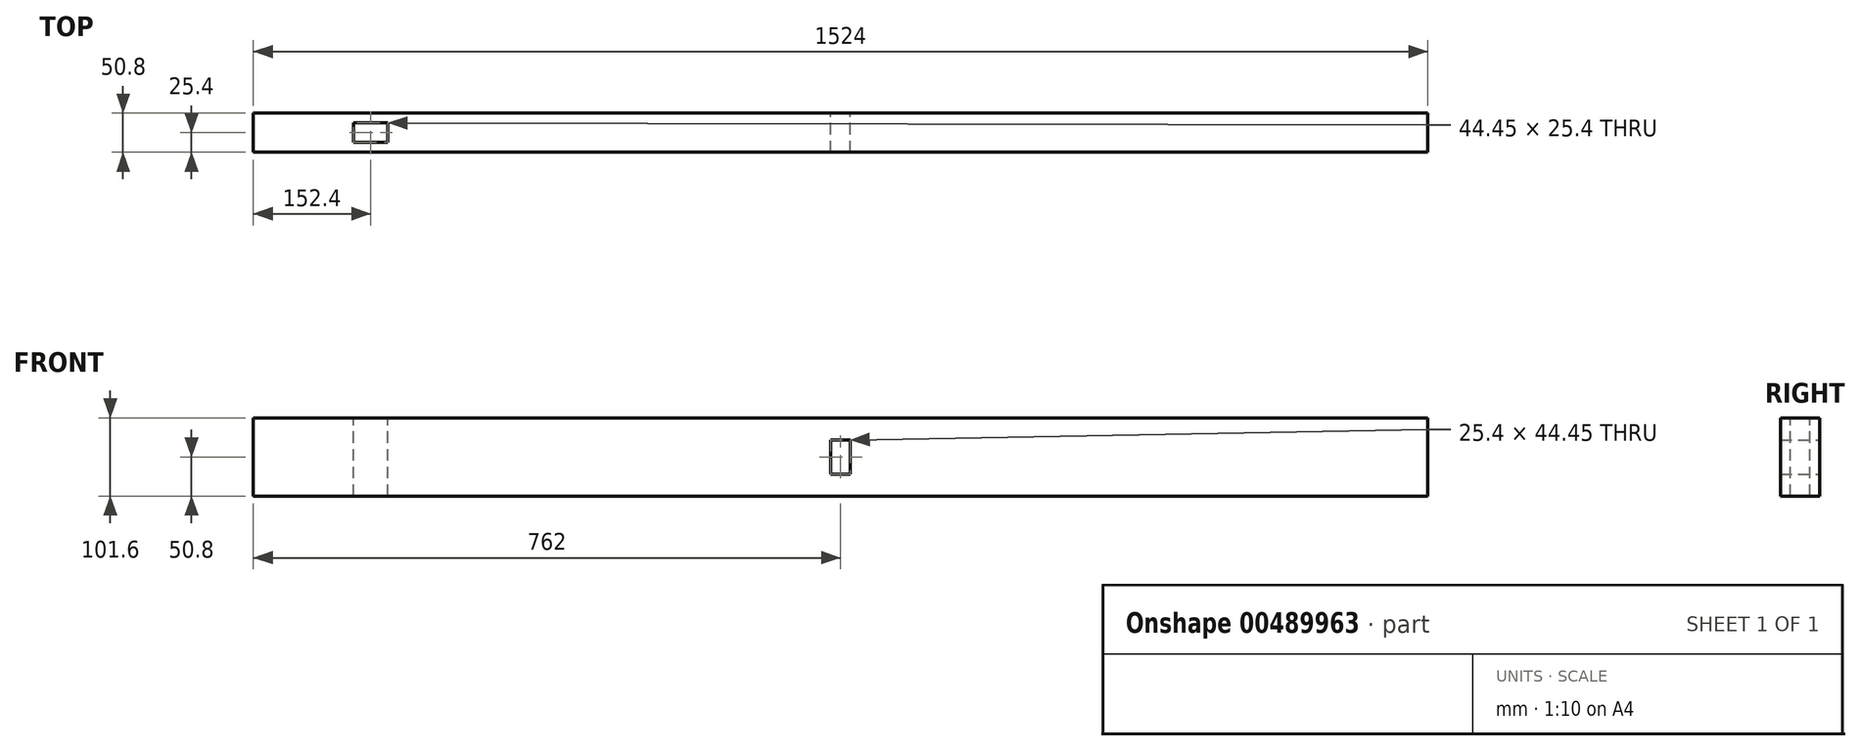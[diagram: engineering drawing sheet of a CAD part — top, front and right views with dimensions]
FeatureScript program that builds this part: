
annotation { "Feature Type Name" : "Feature", "Feature Type Description" : "" }
export const myFeature = defineFeature(function(context is Context, id is Id, definition is map)
    precondition{}
    {
        {
            var Q0;
            Q0=qCreatedBy(makeId("Right.planeOp"),FACE);
            var sketch = newSketch(context, id + "F0", { "sketchPlane" : qUnion([Q0])});
            skLineSegment(sketch, "E0.bottom", {"start": v(-25.4, 50.8) * mm, "end": v(25.4, 50.8) * mm});
            skLineSegment(sketch, "E0.top", {"start": v(-25.4, -50.8) * mm, "end": v(25.4, -50.8) * mm});
            skLineSegment(sketch, "E0.left", {"start": v(-25.4, 50.8) * mm, "end": v(-25.4, -50.8) * mm});
            skLineSegment(sketch, "E0.right", {"start": v(25.4, 50.8) * mm, "end": v(25.4, -50.8) * mm});
            skPoint(sketch, "E0.middle", {"position": v(0, 0) * mm});
            skSolve(sketch);
        }
        {
            var Q0;
            Q0 = qSketchRegion(id + "F0", true);
            extrude(context, id + "F1", {"entities" : qUnion([Q0]), "endBound" : BoundingType.SYMMETRIC, "depth" : 1524 * mm});
        }
        {
            var Q0;
            Q0=makeQuery(id+"F1.opExtrude","SWEPT_FACE",FACE,{"disambiguationData":[OSD([sQuery(id+"F0.wireOp",EDGE,"E0.right")])]});
            var sketch = newSketch(context, id + "F2", { "sketchPlane" : qUnion([Q0])});
            skLineSegment(sketch, "E1.bottom", {"start": v(-12.7, -22.23) * mm, "end": v(12.7, -22.23) * mm});
            skLineSegment(sketch, "E1.top", {"start": v(-12.7, 22.23) * mm, "end": v(12.7, 22.23) * mm});
            skLineSegment(sketch, "E1.left", {"start": v(-12.7, -22.23) * mm, "end": v(-12.7, 22.23) * mm});
            skLineSegment(sketch, "E1.right", {"start": v(12.7, -22.22) * mm, "end": v(12.7, 22.23) * mm});
            skPoint(sketch, "E1.middle", {"position": v(0, 0) * mm});
            skSolve(sketch);
        }
        {
            var Q0;
            Q0 = qSketchRegion(id + "F2", true);
            extrude(context, id + "F3", {"entities" : qUnion([Q0]), "operationType" : NewBodyOperationType.REMOVE, "endBound" : BoundingType.THROUGH_ALL, "oppositeDirection" : true, "depth" : 25.4 * mm});
        }
        {
            var Q0;
            Q0=makeQuery(id+"F1.opExtrude","SWEPT_FACE",FACE,{"disambiguationData":[OSD([sQuery(id+"F0.wireOp",EDGE,"E0.bottom")])]});
            var sketch = newSketch(context, id + "F4", { "sketchPlane" : qUnion([Q0])});
            skLineSegment(sketch, "E2.bottom", {"start": v(-631.82, -12.7) * mm, "end": v(-587.38, -12.7) * mm});
            skLineSegment(sketch, "E2.top", {"start": v(-631.82, 12.7) * mm, "end": v(-587.38, 12.7) * mm});
            skLineSegment(sketch, "E2.left", {"start": v(-631.82, -12.7) * mm, "end": v(-631.82, 12.7) * mm});
            skLineSegment(sketch, "E2.right", {"start": v(-587.38, -12.7) * mm, "end": v(-587.38, 12.7) * mm});
            skPoint(sketch, "E2.middle", {"position": v(-609.6, 0) * mm});
            skSolve(sketch);
        }
        {
            var Q0;
            Q0=makeQuery(id+"F4.imprint","IMPRINT",FACE,{"disambiguationData":[TD([[makeQuery(id+"F4.imprint","IMPRINT",EDGE,{"derivedFrom":sQuery(id+"F4.wireOp",EDGE,"E2.bottom")}),1.0]])]});
            extrude(context, id + "F5", {"entities" : qUnion([Q0]), "operationType" : NewBodyOperationType.REMOVE, "endBound" : BoundingType.THROUGH_ALL, "oppositeDirection" : true, "depth" : 25.4 * mm});
        }
    });
